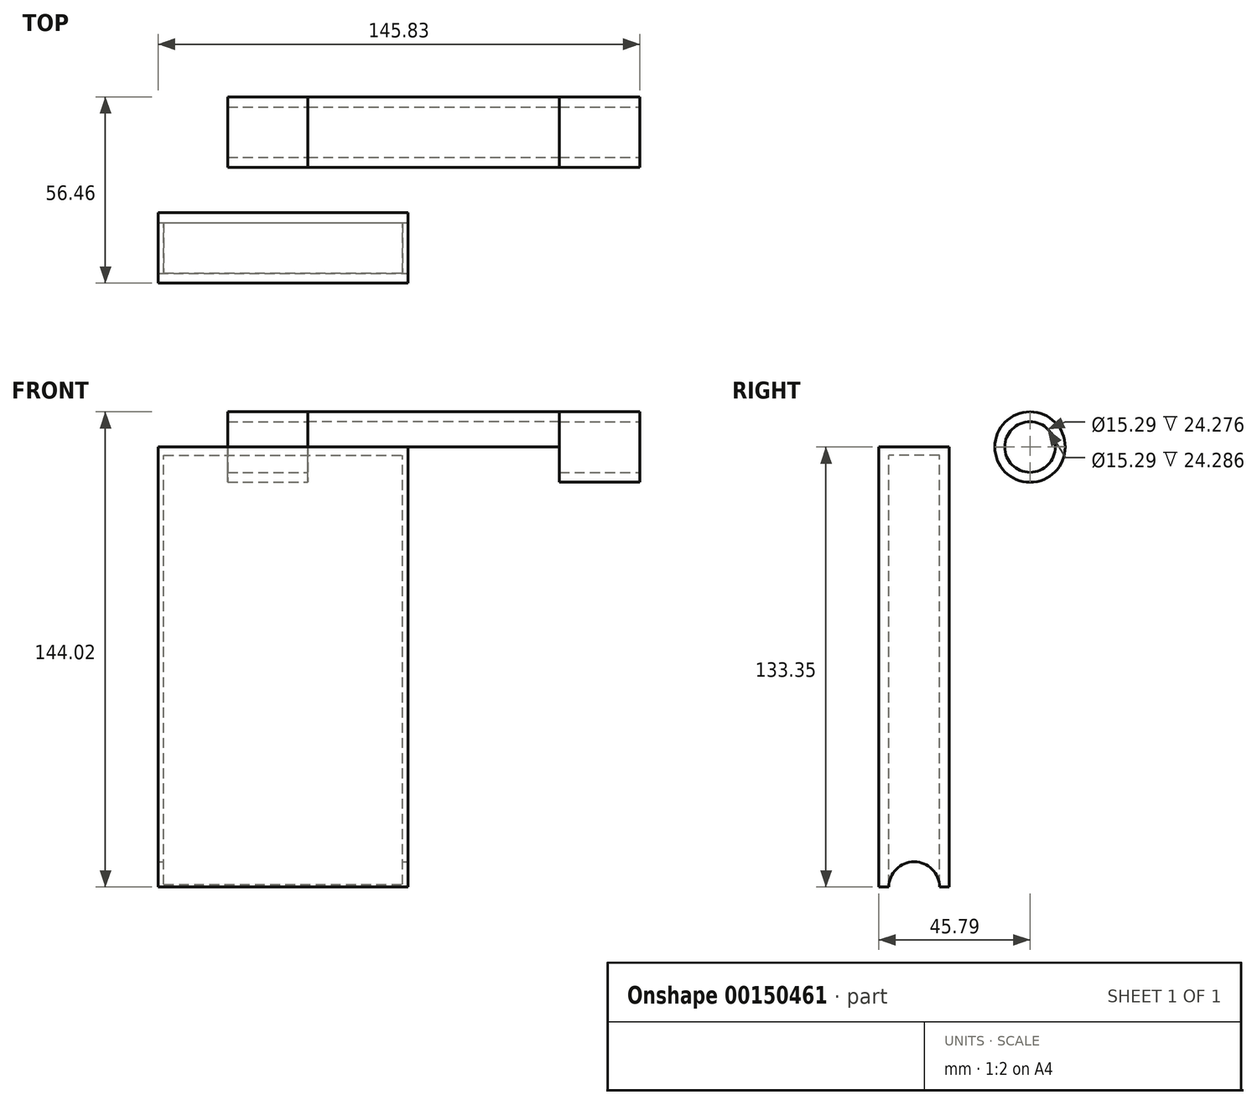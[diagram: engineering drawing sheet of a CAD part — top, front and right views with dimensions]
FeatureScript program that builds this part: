
annotation { "Feature Type Name" : "Feature", "Feature Type Description" : "" }
export const myFeature = defineFeature(function(context is Context, id is Id, definition is map)
    precondition{}
    {
        {
            var Q0;
            Q0=qCreatedBy(makeId("Front.planeOp"),FACE);
            var sketch = newSketch(context, id + "F0", { "sketchPlane" : qUnion([Q0])});
            skLineSegment(sketch, "E0.bottom", {"start": v(-38.1, 10.67) * mm, "end": v(38.1, 10.67) * mm});
            skLineSegment(sketch, "E0.top", {"start": v(-38.1, 7.65) * mm, "end": v(38.1, 7.65) * mm});
            skLineSegment(sketch, "E0.left", {"start": v(-38.1, 10.67) * mm, "end": v(-38.1, 7.65) * mm});
            skLineSegment(sketch, "E0.right", {"start": v(38.1, 10.67) * mm, "end": v(38.1, 7.65) * mm});
            skLineSegment(sketch, "E1", {"start": v(-13.89, 0) * mm, "end": v(26.83, 0) * mm});
            skSolve(sketch);
        }
        {
            var Q0;
            Q0=makeQuery(id+"F0.imprint","IMPRINT",FACE,{"disambiguationData":[TD([[makeQuery(id+"F0.imprint","IMPRINT",EDGE,{"derivedFrom":sQuery(id+"F0.wireOp",EDGE,"E0.bottom")}),-1.0]])]});
            var Q1;
            Q1=sQuery(id+"F0.wireOp",EDGE,"E1");
            revolve(context, id + "F1", {"entities" : qUnion([Q0]), "axis" : qUnion([Q1]), "revolveType" : RevolveType.SYMMETRIC, "angle" : 180 * degree});
        }
        {
            var Q0;
            Q0=qCreatedBy(makeId("Front.planeOp"),FACE);
            var sketch = newSketch(context, id + "F2", { "sketchPlane" : qUnion([Q0])});
            skLineSegment(sketch, "E2.bottom", {"start": v(62.38, 10.67) * mm, "end": v(38.1, 10.67) * mm});
            skLineSegment(sketch, "E2.top", {"start": v(62.38, 7.65) * mm, "end": v(38.1, 7.65) * mm});
            skLineSegment(sketch, "E2.left", {"start": v(62.38, 10.67) * mm, "end": v(62.38, 7.65) * mm});
            skLineSegment(sketch, "E2.right", {"start": v(38.1, 10.67) * mm, "end": v(38.1, 7.65) * mm});
            skLineSegment(sketch, "E3.bottom", {"start": v(-38.1, 10.67) * mm, "end": v(-62.39, 10.67) * mm});
            skLineSegment(sketch, "E3.top", {"start": v(-38.1, 7.65) * mm, "end": v(-62.39, 7.65) * mm});
            skLineSegment(sketch, "E3.left", {"start": v(-38.1, 10.67) * mm, "end": v(-38.1, 7.65) * mm});
            skLineSegment(sketch, "E3.right", {"start": v(-62.39, 10.67) * mm, "end": v(-62.39, 7.65) * mm});
            skLineSegment(sketch, "E4", {"start": v(32.55, 0) * mm, "end": v(-16.72, 0) * mm});
            skSolve(sketch);
        }
        {
            var Q0;
            Q0=makeQuery(id+"F2.imprint","IMPRINT",FACE,{"disambiguationData":[TD([[makeQuery(id+"F2.imprint","IMPRINT",EDGE,{"derivedFrom":sQuery(id+"F2.wireOp",EDGE,"E2.bottom")}),1.0]])]});
            var Q1;
            Q1=makeQuery(id+"F2.imprint","IMPRINT",FACE,{"disambiguationData":[TD([[makeQuery(id+"F2.imprint","IMPRINT",EDGE,{"derivedFrom":sQuery(id+"F2.wireOp",EDGE,"E3.bottom")}),1.0]])]});
            var Q2;
            Q2=sQuery(id+"F2.wireOp",EDGE,"E4");
            revolve(context, id + "F3", {"entities" : qUnion([Q0, Q1]), "axis" : qUnion([Q2]), "revolveType" : RevolveType.FULL});
        }
        {
            var Q0;
            Q0=qCreatedBy(makeId("Top.planeOp"),FACE);
            var sketch = newSketch(context, id + "F4", { "sketchPlane" : qUnion([Q0])});
            skLineSegment(sketch, "E5.bottom", {"start": v(-81.8, -27.47) * mm, "end": v(-9.4, -27.47) * mm});
            skLineSegment(sketch, "E5.top", {"start": v(-81.8, -42.77) * mm, "end": v(-9.4, -42.77) * mm});
            skLineSegment(sketch, "E5.left", {"start": v(-81.8, -27.47) * mm, "end": v(-81.8, -42.77) * mm});
            skLineSegment(sketch, "E5.right", {"start": v(-9.4, -27.47) * mm, "end": v(-9.4, -42.77) * mm});
            skLineSegment(sketch, "E6.bottom", {"start": v(-83.45, -24.45) * mm, "end": v(-7.75, -24.45) * mm});
            skLineSegment(sketch, "E6.top", {"start": v(-83.45, -45.79) * mm, "end": v(-7.75, -45.79) * mm});
            skLineSegment(sketch, "E6.left", {"start": v(-83.45, -24.45) * mm, "end": v(-83.45, -45.79) * mm});
            skLineSegment(sketch, "E6.right", {"start": v(-7.75, -24.45) * mm, "end": v(-7.75, -45.79) * mm});
            skSolve(sketch);
        }
        {
            var Q0;
            Q0=makeQuery(id+"F4.imprint","IMPRINT",FACE,{"disambiguationData":[TD([[makeQuery(id+"F4.imprint","IMPRINT",EDGE,{"derivedFrom":sQuery(id+"F4.wireOp",EDGE,"E5.bottom")}),1.0]])]});
            extrude(context, id + "F5", {"entities" : qUnion([Q0]), "oppositeDirection" : true, "depth" : 133.35 * mm});
        }
        {
            var Q0;
            Q0=makeQuery(id+"F4.imprint","IMPRINT",FACE,{"disambiguationData":[TD([[makeQuery(id+"F4.imprint","IMPRINT",EDGE,{"derivedFrom":sQuery(id+"F4.wireOp",EDGE,"E5.bottom")}),-1.0]])]});
            extrude(context, id + "F6", {"entities" : qUnion([Q0]), "operationType" : NewBodyOperationType.ADD, "oppositeDirection" : true, "depth" : 2.54 * mm});
        }
        {
            var Q0;
            Q0=makeQuery(id+"F5.opExtrude","SWEPT_FACE",FACE,{"disambiguationData":[OSD([sQuery(id+"F4.wireOp",EDGE,"E6.right")])]});
            var sketch = newSketch(context, id + "F7", { "sketchPlane" : qUnion([Q0])});
            skLineSegment(sketch, "E7", {"start": v(-42.77, -133.35) * mm, "end": v(-27.47, -133.35) * mm});
            skPoint(sketch, "E8", {"position": v(-35.12, -133.35) * mm});
            skSolve(sketch);
        }
        {
            var Q0;
            Q0=sQuery(id+"F7.wireOp",VERTEX,"E8");
            var Q1;
            Q1=makeQuery(id+"F5.opExtrude","SWEPT_BODY",BODY,{"disambiguationData":[OSD([sQuery(id+"F4.wireOp",EDGE,"E5.bottom"),sQuery(id+"F4.wireOp",EDGE,"E5.top"),sQuery(id+"F4.wireOp",EDGE,"E5.left"),sQuery(id+"F4.wireOp",EDGE,"E5.right"),sQuery(id+"F4.wireOp",EDGE,"E6.bottom"),sQuery(id+"F4.wireOp",EDGE,"E6.top"),sQuery(id+"F4.wireOp",EDGE,"E6.left"),sQuery(id+"F4.wireOp",EDGE,"E6.right")])]});
            hole(context, id + "F8", {"style" : HoleStyle.SIMPLE, "endStyle" : HoleEndStyle.THROUGH, "holeDiameter" : 15.37 * mm, "locations" : qUnion([Q0]), "scope" : qUnion([Q1]), "isTappedThrough" : true});
        }
    });
